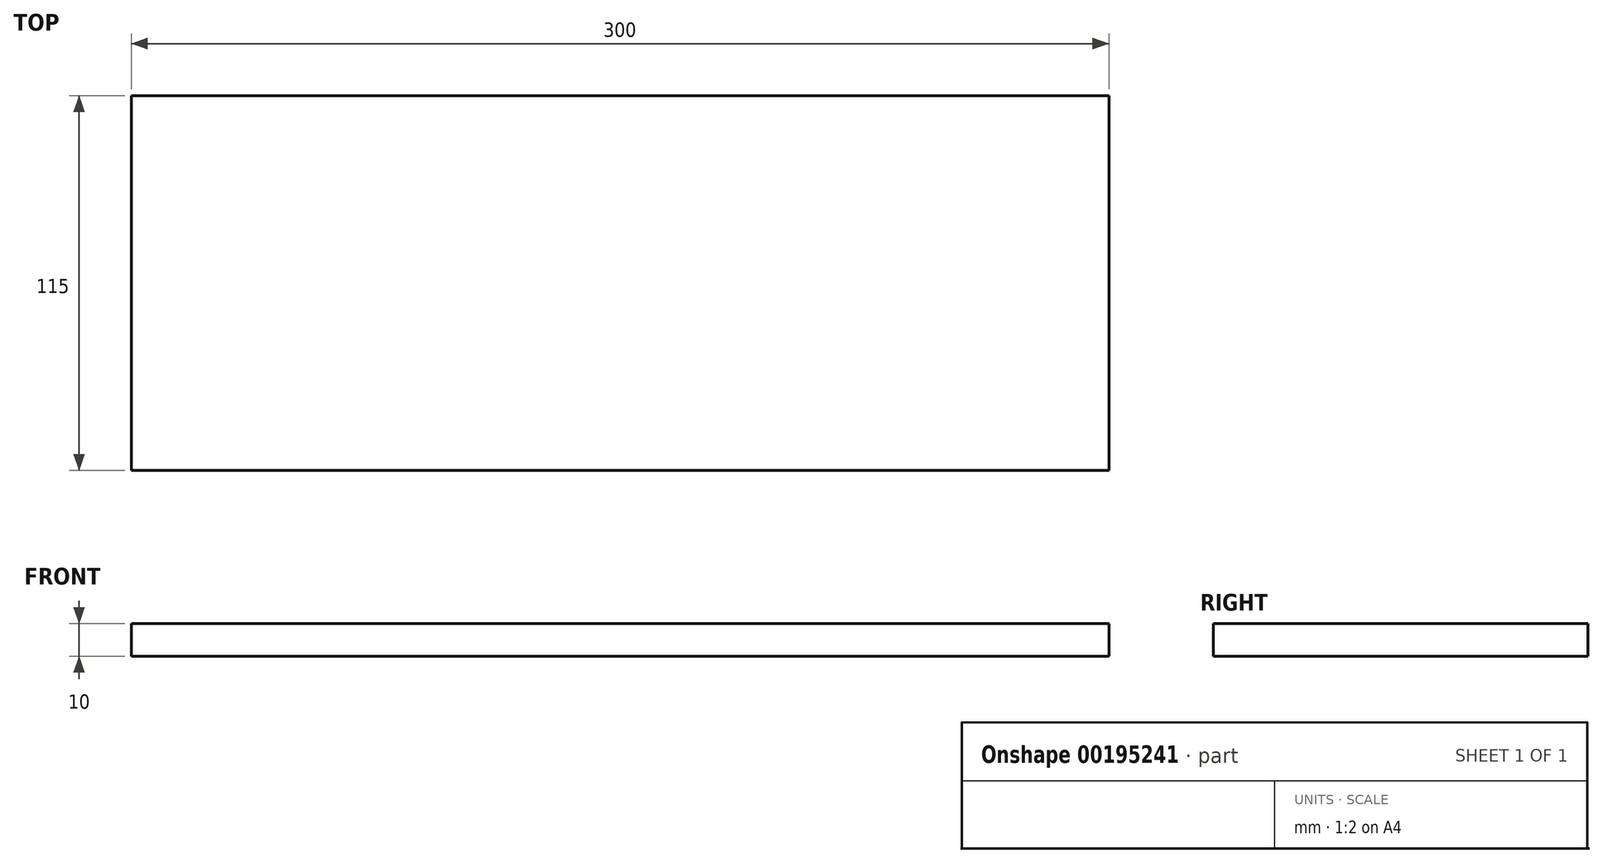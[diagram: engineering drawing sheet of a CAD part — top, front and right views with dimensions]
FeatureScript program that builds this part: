
annotation { "Feature Type Name" : "Feature", "Feature Type Description" : "" }
export const myFeature = defineFeature(function(context is Context, id is Id, definition is map)
    precondition{}
    {
        {
            var Q0;
            Q0=qCreatedBy(makeId("Top.planeOp"),FACE);
            var sketch = newSketch(context, id + "F0", { "sketchPlane" : qUnion([Q0])});
            skLineSegment(sketch, "E0.bottom", {"start": v(-150, 57.5) * mm, "end": v(150, 57.5) * mm});
            skLineSegment(sketch, "E0.top", {"start": v(-150, -57.5) * mm, "end": v(150, -57.5) * mm});
            skLineSegment(sketch, "E0.left", {"start": v(-150, 57.5) * mm, "end": v(-150, -57.5) * mm});
            skLineSegment(sketch, "E0.right", {"start": v(150, 57.5) * mm, "end": v(150, -57.5) * mm});
            skPoint(sketch, "E0.middle", {"position": v(0, 0) * mm});
            skSolve(sketch);
        }
        {
            var Q0;
            Q0=makeQuery(id+"F0.imprint","IMPRINT",FACE,{"disambiguationData":[TD([[makeQuery(id+"F0.imprint","IMPRINT",EDGE,{"derivedFrom":sQuery(id+"F0.wireOp",EDGE,"E0.bottom")}),-1.0]])]});
            extrude(context, id + "F1", {"entities" : qUnion([Q0]), "depth" : 10 * mm});
        }
    });
